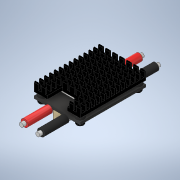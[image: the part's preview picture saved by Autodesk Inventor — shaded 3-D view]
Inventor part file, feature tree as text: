
AUTODESK INVENTOR PART (.ipt)
format: ipt  version: 2020.1 (Build 241239000, 239)  size: 1,066,496 bytes
history: native  units: mm
features: sketch x17, extrude x16, mirror x6, fillet x4, pattern_linear x2, plane x1, revolve x1, chamfer x1, emboss x1, projected_geometry x1
ambient origin geometry x8: Origin, YZ Plane, XZ Plane, XY Plane, X Axis, Y Axis, Z Axis, Center Point
bodies: Solid1 (feature_tree)
feature tree (50):
  extrude  "Extrusion1"  Depth=40.0mm
  extrude  "Extrusion2"  Depth=5.0mm
  extrude  "Extrusion3"  Depth=9.0mm
  extrude  "Extrusion4"  Depth=8.0mm
  extrude  "Extrusion5"  Depth=1.0mm TaperAngle=0.0deg
  fillet  "Fillet1"  Radius=0.2mm
  pattern_linear  "Rectangular Pattern1"  Count1=14 Spacing1=3.0mm
  mirror  "Mirror1"
  extrude  "Extrusion6"  Depth=1.0mm
  fillet  "Fillet2"  Radius=1.0mm
  pattern_linear  "Rectangular Pattern2"  Count1=11 Spacing1=3.0mm
  extrude  "Extrusion7"  Depth=1.0mm TaperAngle=0.0deg
  fillet  "Fillet3"  Radius=1.0mm
  extrude  "Extrusion8"  Depth=1.0mm
  mirror  "Mirror2"
  mirror  "Mirror3"
  sketch  "Sketch9"  dims[d19=0.5mm d20=140.0mm d22=3.0mm]
  extrude  "Extrusion9"  Depth=1.0mm TaperAngle=0.0deg
  fillet  "Fillet4"  Radius=5.0mm
  mirror  "Mirror4"
  plane  "Work Plane1"
  revolve  "Revolution1"  [1 undecoded]
  mirror  "Mirror5"
  mirror  "Mirror6"
  extrude  "Extrusion10"  Depth=0.1mm
  extrude  "Extrusion11"  Depth=0.1mm
  extrude  "Extrusion12"  Depth=0.1mm
  extrude  "Extrusion13"  Depth=0.1mm TaperAngle=0.0deg
  extrude  "Extrusion14"  Depth=0.1mm
  chamfer  "Chamfer1"  Distance=1.24mm
  extrude  "Extrusion15"  Depth=0.1mm
  extrude  "Extrusion16"  Depth=0.1mm
  emboss  "Emboss1"
  sketch  "Sketch14"  dims[d41=1.0mm d42=4.0mm]
  sketch  "Sketch15"  dims[d43=1.0mm d44=1.5mm d45=0.0mm d46=5.0mm]
  sketch  "Sketch16"  dims[d47=8.0mm d48=0.1mm]
  sketch  "Sketch17"  dims[d49=6.0mm d50=4.0mm d51=0.1mm d52=0.5mm d53=3.0mm d54=0.0mm d55=1.999992mm d59=1.24mm d60=2.0mm d61=20.0mm d62=90.0deg d63=2.25mm d64=0.5mm d65=1.0mm d66=1.0mm d67=0.5mm d68=0.5mm d70=0.3mm d71=0.5mm d72=0.5mm d73=0.5mm d74=0.5mm d75=1.48mm d76=1.0mm d77=0.0mm d78=6.0mm d79=0.0mm d80=4.0mm d81=0.0mm d82=1.5mm d83=0.0mm d84=5.0mm d85=0.0mm d86=0.2mm d87=2.0mm d88=45.0deg d89=0.5mm d90=0.5mm d91=1.0mm d92=6.0mm d93=0.0mm d94=1.0mm d95=2.0mm d97=0.5mm d98=2.0mm d99=6.0mm d100=0.0mm d101=1.0mm d102=3.0mm d103=3.0mm d105=0.1mm d106=0.0mm]
  sketch  "Sketch1"  dims[d0=28.0mm d1=40.0mm]
  sketch  "Sketch2"  dims[d2=1.57mm d3=0.0mm d4=5.0mm]
  sketch  "Sketch3"  dims[d5=2.0mm d6=0.0mm d7=9.0mm]
  sketch  "Sketch4"  dims[d8=8.0mm d9=8.0mm]
  projected_geometry  "Projected Loop1"
  sketch  "Sketch5"  dims[d10=2.0mm d11=0.0mm d12=1.0mm d13=0.0mm d14=0.2mm]
  sketch  "Sketch6"  dims[d15=1.0mm]
  sketch  "Sketch7"  dims[d16=2.5mm]
  sketch  "Sketch8"  dims[d17=3.5mm d18=0.0mm]
  sketch  "Sketch10"  dims[d23=20.0mm d25=4.25mm d26=2.5mm d27=1.0mm]
  sketch  "Sketch11"  dims[d28=3.5mm d29=0.0mm]
  sketch  "Sketch12"  dims[d30=0.5mm d31=110.0mm d33=3.0mm d34=30.0mm d36=4.25mm]
  sketch  "Sketch13"  dims[d37=4.5mm d38=2.0mm d39=0.0mm d40=1.0mm]
note: 1 required parameter value undecoded (feature->parameter linkage not recoverable at this tier; creation-order binding heuristic only, values carry confidence <= 0.55)
